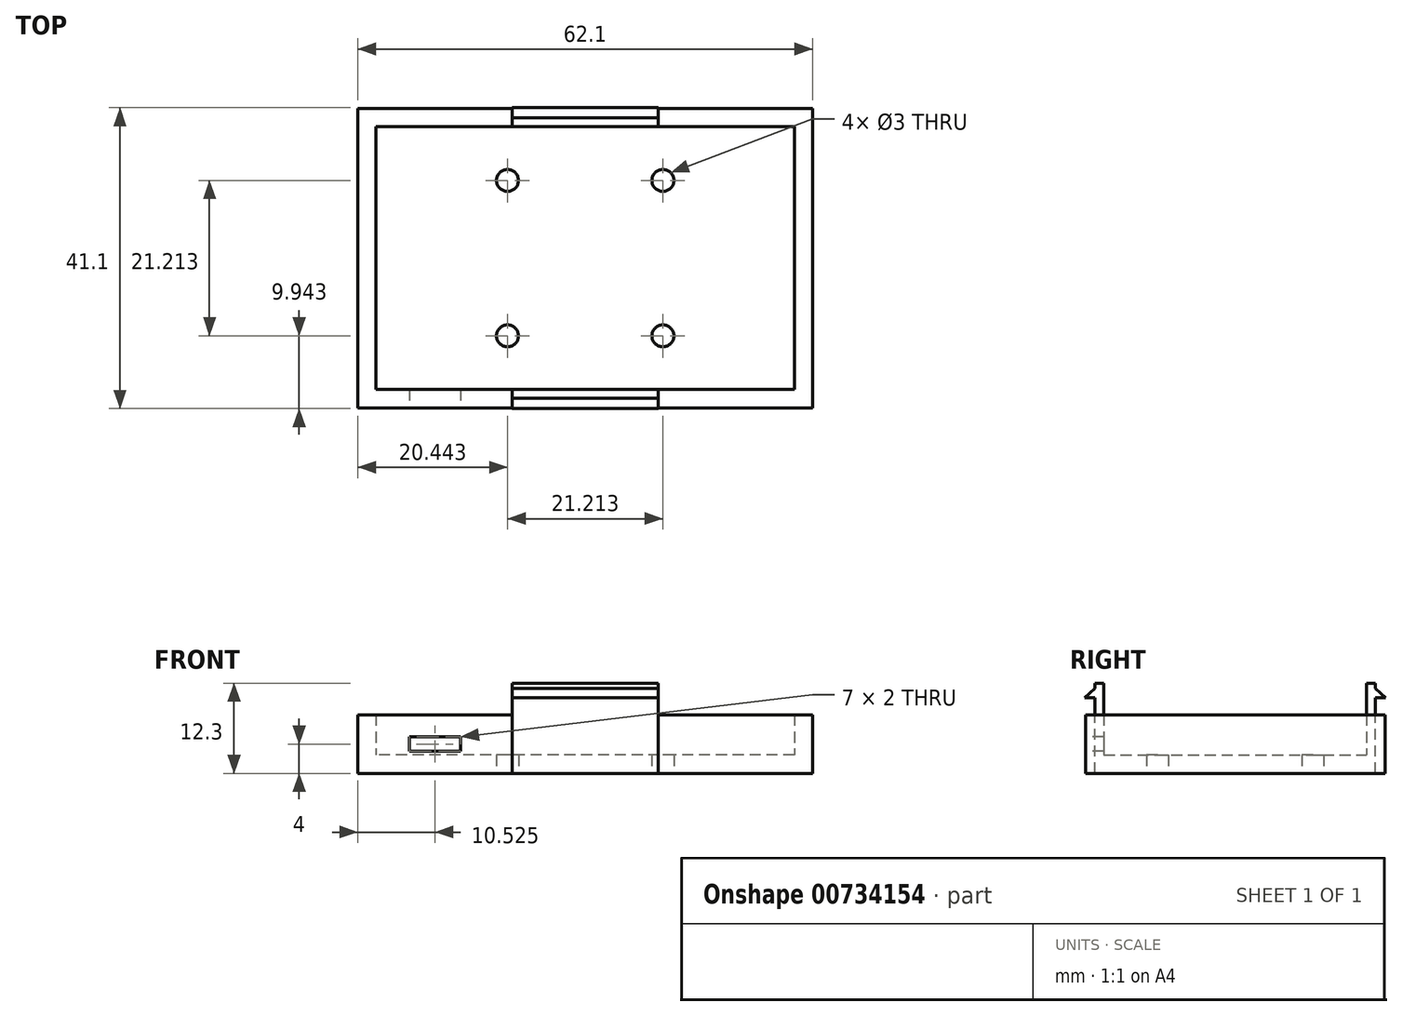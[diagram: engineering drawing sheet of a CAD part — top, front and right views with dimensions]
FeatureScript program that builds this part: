
annotation { "Feature Type Name" : "Feature", "Feature Type Description" : "" }
export const myFeature = defineFeature(function(context is Context, id is Id, definition is map)
    precondition{}
    {
        {
            var Q0;
            Q0=qCreatedBy(makeId("Top.planeOp"),FACE);
            var sketch = newSketch(context, id + "F0", { "sketchPlane" : qUnion([Q0])});
            skLineSegment(sketch, "E0.bottom", {"start": v(31.05, -20.45) * mm, "end": v(-31.05, -20.45) * mm});
            skLineSegment(sketch, "E0.top", {"start": v(31.05, 20.45) * mm, "end": v(-31.05, 20.45) * mm});
            skLineSegment(sketch, "E0.left", {"start": v(31.05, -20.45) * mm, "end": v(31.05, 20.45) * mm});
            skLineSegment(sketch, "E0.right", {"start": v(-31.05, -20.45) * mm, "end": v(-31.05, 20.45) * mm});
            skPoint(sketch, "E0.middle", {"position": v(0, 0) * mm});
            skSolve(sketch);
        }
        {
            var Q0;
            Q0 = qSketchRegion(id + "F0", true);
            extrude(context, id + "F1", {"entities" : qUnion([Q0]), "depth" : 8 * mm, "offsetDistance" : 25 * mm});
        }
        {
            var Q0;
            Q0=makeQuery(id+"F1.opExtrude","CAP_FACE",FACE,{"disambiguationData":[OSD([sQuery(id+"F0.wireOp",EDGE,"E0.bottom"),sQuery(id+"F0.wireOp",EDGE,"E0.top"),sQuery(id+"F0.wireOp",EDGE,"E0.left"),sQuery(id+"F0.wireOp",EDGE,"E0.right")])],"isStart":false});
            shell(context, id + "F2", {"entities" : qUnion([Q0]), "thickness" : 2.5 * mm});
        }
        {
            var Q0;
            Q0=makeQuery(id+"F2.opShell","OFFSET_FACE",FACE,{"disambiguationData":[OSD([sQuery(id+"F0.wireOp",EDGE,"E0.top")])]});
            var sketch = newSketch(context, id + "F3", { "sketchPlane" : qUnion([Q0])});
            skLineSegment(sketch, "E1.bottom", {"start": v(-10, 0) * mm, "end": v(10, 0) * mm});
            skLineSegment(sketch, "E1.top", {"start": v(-10, 12.3) * mm, "end": v(10, 12.3) * mm});
            skLineSegment(sketch, "E1.left", {"start": v(-10, 0) * mm, "end": v(-10, 12.3) * mm});
            skLineSegment(sketch, "E1.right", {"start": v(10, 0) * mm, "end": v(10, 12.3) * mm});
            skPoint(sketch, "E2", {"position": v(0, 0) * mm});
            skSolve(sketch);
        }
        {
            var Q0;
            Q0 = qSketchRegion(id + "F3", true);
            extrude(context, id + "F4", {"entities" : qUnion([Q0]), "operationType" : NewBodyOperationType.ADD, "oppositeDirection" : true, "depth" : 2.6 * mm, "offsetDistance" : 25 * mm});
        }
        {
            var Q0;
            Q0=makeQuery(id+"F4.opExtrude","CAP_FACE",FACE,{"disambiguationData":[OSD([sQuery(id+"F3.wireOp",EDGE,"E1.bottom"),sQuery(id+"F3.wireOp",EDGE,"E1.top"),sQuery(id+"F3.wireOp",EDGE,"E1.left"),sQuery(id+"F3.wireOp",EDGE,"E1.right")])],"isStart":false});
            var sketch = newSketch(context, id + "F5", { "sketchPlane" : qUnion([Q0])});
            skLineSegment(sketch, "E3.bottom", {"start": v(-10, 10.3) * mm, "end": v(10, 10.3) * mm});
            skLineSegment(sketch, "E3.top", {"start": v(-10, 0) * mm, "end": v(10, 0) * mm});
            skLineSegment(sketch, "E3.left", {"start": v(-10, 10.3) * mm, "end": v(-10, 0) * mm});
            skLineSegment(sketch, "E3.right", {"start": v(10, 10.3) * mm, "end": v(10, 0) * mm});
            skSolve(sketch);
        }
        {
            var Q0;
            Q0 = qSketchRegion(id + "F5", true);
            extrude(context, id + "F6", {"entities" : qUnion([Q0]), "operationType" : NewBodyOperationType.REMOVE, "oppositeDirection" : true, "depth" : 1.4 * mm, "offsetDistance" : 25 * mm});
        }
        {
            var Q0;
            Q0=makeQuery(id+"F4.opExtrude","SWEPT_FACE",FACE,{"disambiguationData":[OSD([sQuery(id+"F3.wireOp",EDGE,"E1.right")])]});
            var sketch = newSketch(context, id + "F7", { "sketchPlane" : qUnion([Q0])});
            skLineSegment(sketch, "E4", {"start": v(20.55, 10.3) * mm, "end": v(19.15, 11.58) * mm});
            skLineSegment(sketch, "E5", {"start": v(19.15, 11.58) * mm, "end": v(19.15, 12.3) * mm});
            skLineSegment(sketch, "E6", {"start": v(19.15, 12.3) * mm, "end": v(20.55, 12.3) * mm});
            skLineSegment(sketch, "E7", {"start": v(20.55, 12.3) * mm, "end": v(20.55, 10.3) * mm});
            skSolve(sketch);
        }
        {
            var Q0;
            Q0 = qSketchRegion(id + "F7", true);
            extrude(context, id + "F8", {"entities" : qUnion([Q0]), "operationType" : NewBodyOperationType.REMOVE, "endBound" : BoundingType.UP_TO_NEXT, "oppositeDirection" : true, "depth" : 25 * mm, "offsetDistance" : 25 * mm});
        }
        {
            var Q0;
            Q0=makeQuery(id+"F2.opShell","OFFSET_FACE",FACE,{"disambiguationData":[OSD([sQuery(id+"F0.wireOp",EDGE,"E0.bottom"),sQuery(id+"F0.wireOp",EDGE,"E0.top"),sQuery(id+"F0.wireOp",EDGE,"E0.left"),sQuery(id+"F0.wireOp",EDGE,"E0.right")])]});
            var sketch = newSketch(context, id + "F9", { "sketchPlane" : qUnion([Q0])});
            skLineSegment(sketch, "E8.bottom", {"start": v(39.65, 0) * mm, "end": v(-41.73, 0) * mm});
            skLineSegment(sketch, "E8.top", {"start": v(39.65, -28.72) * mm, "end": v(-41.73, -28.72) * mm});
            skLineSegment(sketch, "E8.left", {"start": v(39.65, 0) * mm, "end": v(39.65, -28.72) * mm});
            skLineSegment(sketch, "E8.right", {"start": v(-41.73, 0) * mm, "end": v(-41.73, -28.72) * mm});
            skSolve(sketch);
        }
        {
            var Q0;
            Q0 = qSketchRegion(id + "F9", true);
            extrude(context, id + "F10", {"entities" : qUnion([Q0]), "operationType" : NewBodyOperationType.REMOVE, "endBound" : BoundingType.THROUGH_ALL, "oppositeDirection" : true, "depth" : 25 * mm, "offsetDistance" : 25 * mm, "hasSecondDirection" : true, "secondDirectionBound" : SecondDirectionBoundingType.THROUGH_ALL, "secondDirectionOppositeDirection" : false, "secondDirectionDepth" : 25 * mm});
        }
        {
            var Q0;
            Q0=makeQuery(id+"F1.opExtrude","SWEPT_BODY",BODY,{"disambiguationData":[OSD([sQuery(id+"F0.wireOp",EDGE,"E0.bottom"),sQuery(id+"F0.wireOp",EDGE,"E0.top"),sQuery(id+"F0.wireOp",EDGE,"E0.left"),sQuery(id+"F0.wireOp",EDGE,"E0.right")])]});
            var Q1;
            Q1=qCreatedBy(makeId("Front.planeOp"),FACE);
            mirror(context, id + "F11", {"operationType" : NewBodyOperationType.ADD, "entities" : qUnion([Q0]), "mirrorPlane" : qUnion([Q1])});
        }
        {
            var Q0;
            {var subQ0=sQuery(id+"F0.wireOp",EDGE,"E0.right");var subQ2=sQuery(id+"F0.wireOp",EDGE,"E0.top");Q0=makeQuery(id+"F11.opPattern","COPY",FACE,{"derivedFrom":makeQuery(id+"F4.boolean.opBoolean","SPLIT",FACE,{"disambiguationData":[TD([makeQuery(id+"F1.opExtrude","SWEPT_FACE",FACE,{"disambiguationData":[OSD([subQ0])]})])],"derivedFrom":makeQuery(id+"F1.opExtrude","SWEPT_FACE",FACE,{"disambiguationData":[OSD([subQ2])]})}),"instanceName":"1"});}
            var sketch = newSketch(context, id + "F12", { "sketchPlane" : qUnion([Q0])});
            skLineSegment(sketch, "E9.bottom", {"start": v(-24.03, 5) * mm, "end": v(-17.03, 5) * mm});
            skLineSegment(sketch, "E9.top", {"start": v(-24.03, 3) * mm, "end": v(-17.03, 3) * mm});
            skLineSegment(sketch, "E9.left", {"start": v(-24.03, 5) * mm, "end": v(-24.03, 3) * mm});
            skLineSegment(sketch, "E9.right", {"start": v(-17.03, 5) * mm, "end": v(-17.03, 3) * mm});
            skPoint(sketch, "E10", {"position": v(-31.05, 4) * mm});
            skLineSegment(sketch, "E11", {"start": v(-31.05, 4) * mm, "end": v(-10, 4) * mm, "construction": true});
            skPoint(sketch, "E12", {"position": v(-24.03, 4) * mm});
            skPoint(sketch, "E13", {"position": v(-17.03, 4) * mm});
            skPoint(sketch, "E14", {"position": v(-20.52, 8) * mm});
            skLineSegment(sketch, "E15", {"start": v(-20.52, 8) * mm, "end": v(-20.52, 0) * mm, "construction": true});
            skPoint(sketch, "E16", {"position": v(-20.53, 5) * mm});
            skSolve(sketch);
        }
        {
            var Q0;
            Q0 = qSketchRegion(id + "F12", true);
            extrude(context, id + "F13", {"entities" : qUnion([Q0]), "operationType" : NewBodyOperationType.REMOVE, "endBound" : BoundingType.UP_TO_NEXT, "oppositeDirection" : true, "depth" : 25 * mm, "offsetDistance" : 25 * mm});
        }
        {
            var Q0;
            {var subQ0=makeQuery(id+"F4.boolean.opBoolean","MERGE",FACE,{"derivedFrom":[makeQuery(id+"F1.opExtrude","CAP_FACE",FACE,{"disambiguationData":[OSD([sQuery(id+"F0.wireOp",EDGE,"E0.bottom"),sQuery(id+"F0.wireOp",EDGE,"E0.top"),sQuery(id+"F0.wireOp",EDGE,"E0.left"),sQuery(id+"F0.wireOp",EDGE,"E0.right")])],"isStart":true}),makeQuery(id+"F4.opExtrude","SWEPT_FACE",FACE,{"disambiguationData":[OSD([sQuery(id+"F3.wireOp",EDGE,"E1.bottom")])]})]});Q0=makeQuery(id+"F11.boolean.opBoolean","MERGE",FACE,{"derivedFrom":[subQ0,makeQuery(id+"F11.opPattern","COPY",FACE,{"derivedFrom":subQ0,"instanceName":"1"})]});}
            var sketch = newSketch(context, id + "F14", { "sketchPlane" : qUnion([Q0])});
            skCircle(sketch, "E17", {"center": v(-10.6, 10.6) * mm, "radius": 1.5 * mm});
            skLineSegment(sketch, "E18", {"start": v(-10.6, 10.6) * mm, "end": v(0, 0) * mm, "construction": true});
            skCircle(sketch, "E19.1.0", {"center": v(10.6, 10.6) * mm, "radius": 1.5 * mm});
            skCircle(sketch, "E19.2.0", {"center": v(10.6, -10.6) * mm, "radius": 1.5 * mm});
            skCircle(sketch, "E19.3.0", {"center": v(-10.6, -10.6) * mm, "radius": 1.5 * mm});
            skPoint(sketch, "E19.center", {"position": v(0, 0) * mm});
            skLineSegment(sketch, "E19.anchor1", {"start": v(0, 0) * mm, "end": v(-10.6, 10.6) * mm, "construction": true});
            skLineSegment(sketch, "E19.anchor2", {"start": v(0, 0) * mm, "end": v(-10.6, -10.6) * mm, "construction": true});
            skSolve(sketch);
        }
        {
            var Q0;
            Q0=makeQuery(id+"F14.imprint","IMPRINT",FACE,{"disambiguationData":[TD([[makeQuery(id+"F14.imprint","IMPRINT",EDGE,{"derivedFrom":sQuery(id+"F14.wireOp",EDGE,"E17")}),1.0]])]});
            var Q1;
            Q1=makeQuery(id+"F14.imprint","IMPRINT",FACE,{"disambiguationData":[TD([[makeQuery(id+"F14.imprint","IMPRINT",EDGE,{"derivedFrom":sQuery(id+"F14.wireOp",EDGE,"E19.1.0")}),1.0]])]});
            var Q2;
            Q2=makeQuery(id+"F14.imprint","IMPRINT",FACE,{"disambiguationData":[TD([[makeQuery(id+"F14.imprint","IMPRINT",EDGE,{"derivedFrom":sQuery(id+"F14.wireOp",EDGE,"E19.2.0")}),1.0]])]});
            var Q3;
            Q3=makeQuery(id+"F14.imprint","IMPRINT",FACE,{"disambiguationData":[TD([[makeQuery(id+"F14.imprint","IMPRINT",EDGE,{"derivedFrom":sQuery(id+"F14.wireOp",EDGE,"E19.3.0")}),1.0]])]});
            extrude(context, id + "F15", {"entities" : qUnion([Q0, Q1, Q2, Q3]), "operationType" : NewBodyOperationType.REMOVE, "endBound" : BoundingType.UP_TO_NEXT, "oppositeDirection" : true, "depth" : 25 * mm, "offsetDistance" : 25 * mm});
        }
    });
